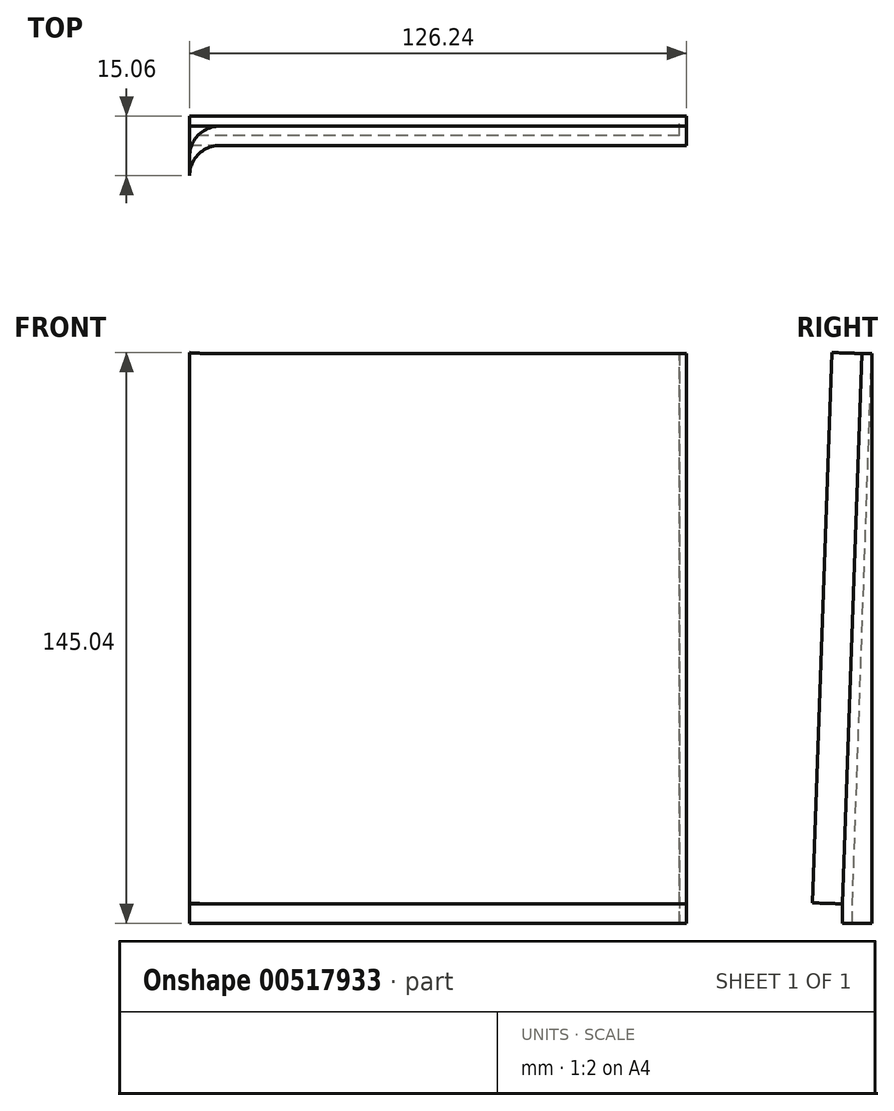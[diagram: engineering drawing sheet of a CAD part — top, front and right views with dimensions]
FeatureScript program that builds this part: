
annotation { "Feature Type Name" : "Feature", "Feature Type Description" : "" }
export const myFeature = defineFeature(function(context is Context, id is Id, definition is map)
    precondition{}
    {
        {
            var Q0;
            Q0=qCreatedBy(makeId("Front.planeOp"),FACE);
            var sketch = newSketch(context, id + "F0", { "sketchPlane" : qUnion([Q0])});
            skLineSegment(sketch, "E0", {"start": v(40.4, 96.23) * mm, "end": v(-85.85, 96.23) * mm});
            skLineSegment(sketch, "E1", {"start": v(-85.85, 96.23) * mm, "end": v(-85.85, -60.5) * mm});
            skLineSegment(sketch, "E2", {"start": v(-85.85, -60.5) * mm, "end": v(40.4, -60.5) * mm});
            skLineSegment(sketch, "E3", {"start": v(40.4, -60.5) * mm, "end": v(40.4, 96.23) * mm});
            skSolve(sketch);
        }
        {
            var Q0;
            Q0=makeQuery(id+"F0.imprint","IMPRINT",FACE,{"disambiguationData":[TD([[makeQuery(id+"F0.imprint","IMPRINT",EDGE,{"derivedFrom":sQuery(id+"F0.wireOp",EDGE,"E0")}),1.0]])]});
            extrude(context, id + "F1", {"entities" : qUnion([Q0]), "depth" : 25.4 * mm, "offsetDistance" : 25.4 * mm});
        }
        {
            var Q0;
            Q0=makeQuery(id+"F1.opExtrude","SWEPT_FACE",FACE,{"disambiguationData":[OSD([sQuery(id+"F0.wireOp",EDGE,"E1")])]});
            var sketch = newSketch(context, id + "F2", { "sketchPlane" : qUnion([Q0])});
            skLineSegment(sketch, "E4", {"start": v(2.54, 84.29) * mm, "end": v(0, 84.29) * mm});
            skPoint(sketch, "E5", {"position": v(7.45, -55.54) * mm});
            skPoint(sketch, "E6", {"position": v(4.9, -55.54) * mm});
            skLineSegment(sketch, "E7", {"start": v(7.45, -55.54) * mm, "end": v(2.54, 84.29) * mm});
            skLineSegment(sketch, "E8", {"start": v(7.45, -55.54) * mm, "end": v(4.9, -55.54) * mm});
            skLineSegment(sketch, "E9", {"start": v(4.9, -55.54) * mm, "end": v(0, 84.29) * mm});
            skLineSegment(sketch, "E10", {"start": v(7.45, -60.5) * mm, "end": v(7.45, -55.54) * mm});
            skLineSegment(sketch, "E11", {"start": v(4.9, -60.5) * mm, "end": v(4.9, -55.54) * mm});
            skLineSegment(sketch, "E12", {"start": v(4.9, -60.5) * mm, "end": v(7.45, -60.5) * mm});
            skSolve(sketch);
        }
        {
            var Q0;
            Q0=makeQuery(id+"F2.imprint","IMPRINT",FACE,{"disambiguationData":[TD([[makeQuery(id+"F2.imprint","IMPRINT",EDGE,{"derivedFrom":sQuery(id+"F2.wireOp",EDGE,"E9")}),1.0]])]});
            extrude(context, id + "F3", {"entities" : qUnion([Q0]), "operationType" : NewBodyOperationType.REMOVE, "oppositeDirection" : true, "depth" : 124.46 * mm, "offsetDistance" : 25.4 * mm});
        }
        {
            var Q0;
            {var subQ3=sQuery(id+"F2.wireOp",EDGE,"E7");Q0=makeQuery(id+"F2.imprint","IMPRINT",FACE,{"disambiguationData":[TD([[makeQuery(id+"F2.imprint","IMPRINT",EDGE,{"derivedFrom":subQ3}),-1.0]])]});}
            extrude(context, id + "F4", {"entities" : qUnion([Q0]), "operationType" : NewBodyOperationType.REMOVE, "oppositeDirection" : true, "depth" : 152.4 * mm, "offsetDistance" : 25.4 * mm});
        }
        {
            var Q0;
            Q0=makeQuery(id+"F4.boolean.opBoolean","COPY",FACE,{"derivedFrom":makeQuery(id+"F4.opExtrude","SWEPT_FACE",FACE,{"disambiguationData":[OSD([sQuery(id+"F2.wireOp",EDGE,"E7")])]})});
            var sketch = newSketch(context, id + "F5", { "sketchPlane" : qUnion([Q0])});
            skLineSegment(sketch, "E13", {"start": v(-85.85, 84.15) * mm, "end": v(-85.85, -55.77) * mm});
            skLineSegment(sketch, "E14", {"start": v(-85.85, 84.15) * mm, "end": v(-78.23, 84.15) * mm});
            skLineSegment(sketch, "E15", {"start": v(-78.23, 84.15) * mm, "end": v(-78.23, -55.77) * mm});
            skLineSegment(sketch, "E16", {"start": v(-78.23, -55.77) * mm, "end": v(-85.85, -55.77) * mm});
            skSolve(sketch);
        }
        {
            var Q0;
            Q0=makeQuery(id+"F5.imprint","IMPRINT",FACE,{"disambiguationData":[TD([[makeQuery(id+"F5.imprint","IMPRINT",EDGE,{"derivedFrom":sQuery(id+"F5.wireOp",EDGE,"E13")}),-1.0]])]});
            extrude(context, id + "F6", {"entities" : qUnion([Q0]), "operationType" : NewBodyOperationType.ADD, "depth" : 7.62 * mm, "offsetDistance" : 25.4 * mm});
        }
        {
            var Q0;
            Q0=makeQuery(id+"F6.opExtrude","SWEPT_FACE",FACE,{"disambiguationData":[OSD([sQuery(id+"F5.wireOp",EDGE,"E14")])]});
            var sketch = newSketch(context, id + "F7", { "sketchPlane" : qUnion([Q0])});
            skArc(sketch, "E17", {"start": v(-78.23, -5.5) * mm, "mid": v(-83.61, -7.73) * mm, "end": v(-85.85, -13.11) * mm});
            skSolve(sketch);
        }
        {
            var Q0;
            Q0=makeQuery(id+"F7.imprint","IMPRINT",FACE,{"disambiguationData":[TD([[makeQuery(id+"F7.imprint","IMPRINT",EDGE,{"derivedFrom":sQuery(id+"F7.wireOp",EDGE,"E17")}),1.0]])]});
            extrude(context, id + "F8", {"entities" : qUnion([Q0]), "operationType" : NewBodyOperationType.REMOVE, "oppositeDirection" : true, "depth" : 152.4 * mm, "offsetDistance" : 25.4 * mm});
        }
    });
